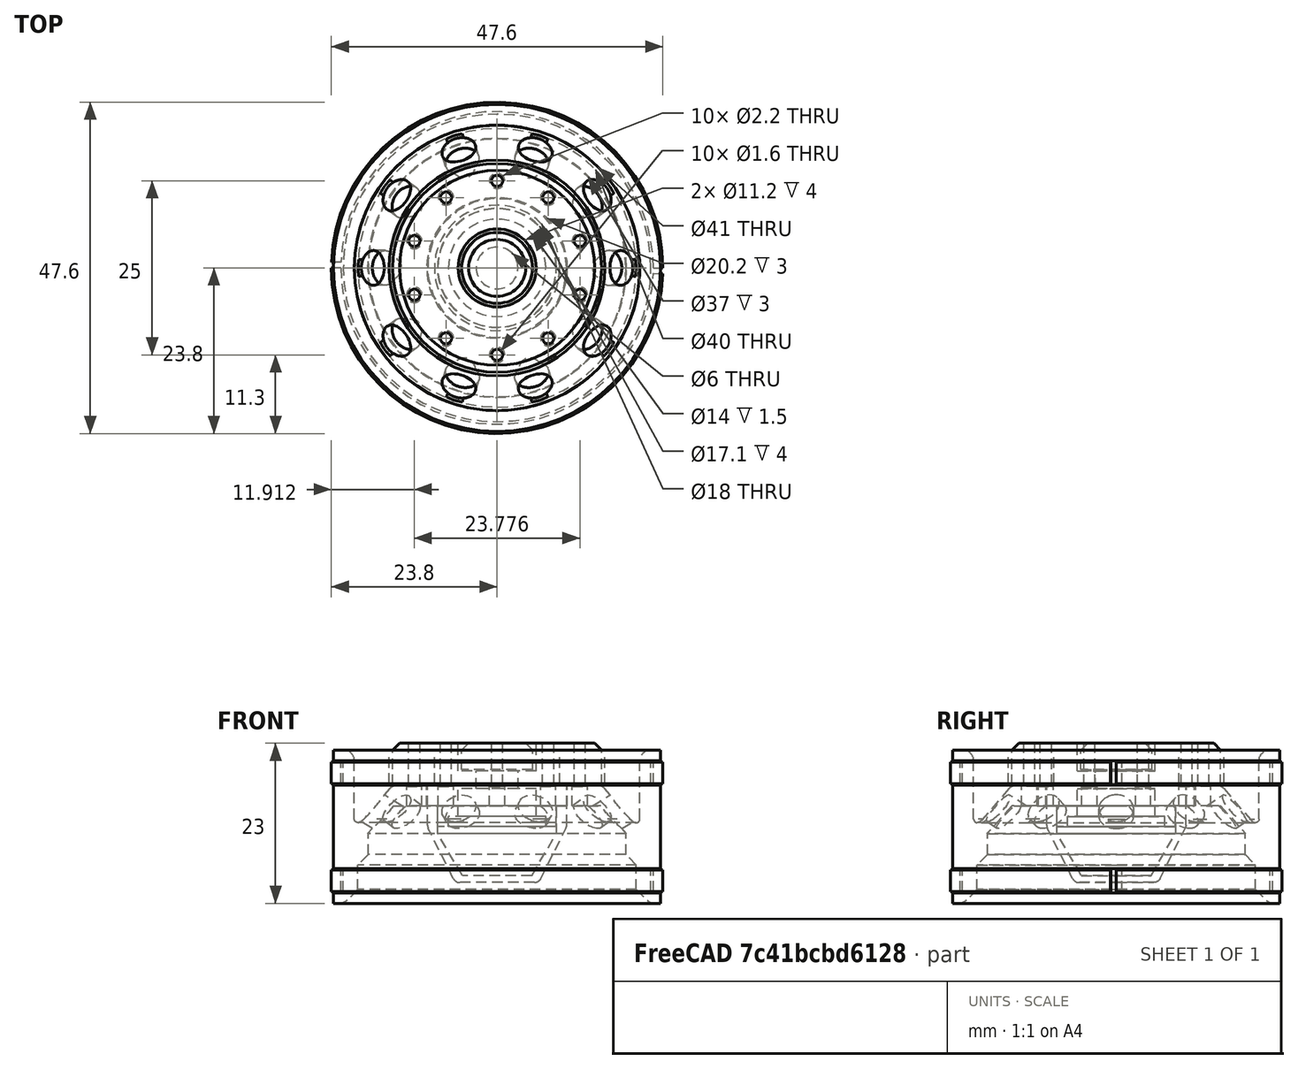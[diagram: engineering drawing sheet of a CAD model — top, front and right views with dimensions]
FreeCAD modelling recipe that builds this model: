
FCSTD DOCUMENT  (FreeCAD 0.19R)
Label: wheels-wide
License: All rights reserved
LicenseURL: http://en.wikipedia.org/wiki/All_rights_reserved
objects: Part::Cylinder×69, Part::MultiFuse×34, Part::Cut×23, Part::Mirroring×5, Part::Fillet×5, Part::Cone×4, Part::Chamfer×4, App::DocumentObjectGroup×1
note: 144 computed .brp shape members not serialized (recipe doc carries the construction recipe); baked Part::Feature solids carry a one-line shape summary decoded from their .brp

FEATURE [Part::Cylinder] Cylinder073
  Angle = 360
  AttacherType = Attacher::AttachEngine3D
  Height = 22
  Radius = 23.5
FEATURE [Part::Cylinder] Cylinder074
  Angle = 360
  AttacherType = Attacher::AttachEngine3D
  Height = 19
  Radius = 23.5
FEATURE [Part::Cylinder] Cylinder075
  Angle = 360
  AttacherType = Attacher::AttachEngine3D
  Height = 19
  Radius = 22.1
FEATURE [Part::Cut] Cut022
  Base = -> Cylinder074
  Placement = pos=(0,0,1.5) rot=(0,0,1;0rad)
  Refine = true
  Tool = -> Cylinder075
FEATURE [Part::Cut] Cut023
  Base = -> Cylinder073
  Refine = true
  Tool = -> Cut022
FEATURE [Part::Cylinder] Cylinder076
  Angle = 360
  AttacherType = Attacher::AttachEngine3D
  Height = 12
  Radius = 22
FEATURE [Part::Cylinder] Cylinder077
  Angle = 360
  AttacherType = Attacher::AttachEngine3D
  Height = 12
  Placement = pos=(0,0,0.5) rot=(0,0,1;0rad)
  Radius = 23.5
FEATURE [Part::Cut] Cut024
  Base = -> Cylinder077
  Placement = pos=(0,0,4.5) rot=(0,0,1;0rad)
  Refine = true
  Tool = -> Cylinder076
FEATURE [Part::Cylinder] Cylinder078
  Angle = 360
  AttacherType = Attacher::AttachEngine3D
  Height = 22
  Radius = 18.5
FEATURE [Part::MultiFuse] Fusion014
  Refine = true
  Shapes = -> [Cut024,Cut023]
FEATURE [Part::Cut] Cut025
  Base = -> Fusion014
  Refine = true
  Tool = -> Cylinder078
FEATURE [Part::Cone] Cone002
  Angle = 360
  AttacherType = Attacher::AttachEngine3D
  Height = 7
  Placement = pos=(0,0,15) rot=(0,0,1;0rad)
  Radius1 = 21
  Radius2 = 15
FEATURE [Part::Cylinder] Cylinder079
  Angle = 360
  AttacherType = Attacher::AttachEngine3D
  Height = 12
  Placement = pos=(0,0,10) rot=(0,0,1;0rad)
  Radius = 20.5
FEATURE [Part::Cylinder] Cylinder080
  Angle = 360
  AttacherType = Attacher::AttachEngine3D
  Height = 7
  Radius = 20
FEATURE [Part::Cylinder] Cylinder081
  Angle = 360
  AttacherType = Attacher::AttachEngine3D
  Height = 26
  Radius = 10
FEATURE [Part::Cylinder] Cylinder082
  Angle = 360
  AttacherType = Attacher::AttachEngine3D
  Height = 8
  Placement = pos=(12,0,16) rot=(0,1,0;1.01229rad)
  Radius = 2.5
FEATURE [Part::Mirroring] Part__Mirroring005  label="Cylinder107 (Mirror #1)009"
  Base = (0,0,0)
  Normal = (1,0,0)
  Source = -> Cylinder082
FEATURE [Part::Cylinder] Cylinder083
  Angle = 360
  AttacherType = Attacher::AttachEngine3D
  Height = 8
  Placement = pos=(12,0,16) rot=(0,1,0;1.01229rad)
  Radius = 2.5
FEATURE [Part::MultiFuse] Fusion015
  Refine = true
  Shapes = -> [Cylinder083,Part__Mirroring005]
FEATURE [Part::Cylinder] Cylinder084
  Angle = 360
  AttacherType = Attacher::AttachEngine3D
  Height = 8
  Placement = pos=(12,0,16) rot=(0,1,0;1.01229rad)
  Radius = 2.5
FEATURE [Part::Cylinder] Cylinder085
  Angle = 360
  AttacherType = Attacher::AttachEngine3D
  Height = 8
  Placement = pos=(12,0,16) rot=(0,1,0;1.01229rad)
  Radius = 2.5
FEATURE [Part::Mirroring] Part__Mirroring006  label="Cylinder107 (Mirror #1)010"
  Base = (0,0,0)
  Normal = (1,0,0)
  Source = -> Cylinder085
FEATURE [Part::MultiFuse] Fusion016
  Placement = pos=(0,0,0) rot=(0,0,1;0.628319rad)
  Refine = true
  Shapes = -> [Cylinder084,Part__Mirroring006]
FEATURE [Part::Cylinder] Cylinder086
  Angle = 360
  AttacherType = Attacher::AttachEngine3D
  Height = 8
  Placement = pos=(12,0,16) rot=(0,1,0;1.01229rad)
  Radius = 2.5
FEATURE [Part::Cylinder] Cylinder087
  Angle = 360
  AttacherType = Attacher::AttachEngine3D
  Height = 8
  Placement = pos=(12,0,16) rot=(0,1,0;1.01229rad)
  Radius = 2.5
FEATURE [Part::Mirroring] Part__Mirroring007  label="Cylinder107 (Mirror #1)011"
  Base = (0,0,0)
  Normal = (1,0,0)
  Source = -> Cylinder087
FEATURE [Part::MultiFuse] Fusion017
  Placement = pos=(0,0,0) rot=(0,0,1;1.25664rad)
  Refine = true
  Shapes = -> [Cylinder086,Part__Mirroring007]
FEATURE [Part::Cylinder] Cylinder088
  Angle = 360
  AttacherType = Attacher::AttachEngine3D
  Height = 8
  Placement = pos=(12,0,16) rot=(0,1,0;1.01229rad)
  Radius = 2.5
FEATURE [Part::Cylinder] Cylinder089
  Angle = 360
  AttacherType = Attacher::AttachEngine3D
  Height = 8
  Placement = pos=(12,0,16) rot=(0,1,0;1.01229rad)
  Radius = 2.5
FEATURE [Part::Mirroring] Part__Mirroring008  label="Cylinder107 (Mirror #1)012"
  Base = (0,0,0)
  Normal = (1,0,0)
  Source = -> Cylinder089
FEATURE [Part::MultiFuse] Fusion018
  Placement = pos=(0,0,0) rot=(0,0,1;1.88496rad)
  Refine = true
  Shapes = -> [Cylinder088,Part__Mirroring008]
FEATURE [Part::Cylinder] Cylinder090
  Angle = 360
  AttacherType = Attacher::AttachEngine3D
  Height = 8
  Placement = pos=(12,0,16) rot=(0,1,0;1.01229rad)
  Radius = 2.5
FEATURE [Part::Cylinder] Cylinder091
  Angle = 360
  AttacherType = Attacher::AttachEngine3D
  Height = 8
  Placement = pos=(12,0,16) rot=(0,1,0;1.01229rad)
  Radius = 2.5
FEATURE [Part::Mirroring] Part__Mirroring009  label="Cylinder107 (Mirror #1)013"
  Base = (0,0,0)
  Normal = (1,0,0)
  Source = -> Cylinder091
FEATURE [Part::MultiFuse] Fusion019
  Placement = pos=(0,0,0) rot=(0,0,1;2.51327rad)
  Refine = true
  Shapes = -> [Cylinder090,Part__Mirroring009]
FEATURE [Part::MultiFuse] Fusion020
  Placement = pos=(0,0,-6) rot=(0,0,1;0rad)
  Refine = true
  Shapes = -> [Fusion015,Fusion016,Fusion017,Fusion018,Fusion019]
FEATURE [Part::Cylinder] Cylinder092
  Angle = 360
  AttacherType = Attacher::AttachEngine3D
  Height = 10
  Placement = pos=(12.5,0,13) rot=(0,0,1;0rad)
  Radius = 1.1
FEATURE [Part::Cylinder] Cylinder093
  Angle = 360
  AttacherType = Attacher::AttachEngine3D
  Height = 10
  Placement = pos=(-12.5,0,13) rot=(0,0,1;0rad)
  Radius = 1.1
FEATURE [Part::MultiFuse] Fusion021
  Placement = pos=(0,0,0) rot=(0,0,1;0.314159rad)
  Refine = true
  Shapes = -> [Cylinder092,Cylinder093]
FEATURE [Part::Cylinder] Cylinder094
  Angle = 360
  AttacherType = Attacher::AttachEngine3D
  Height = 10
  Placement = pos=(12.5,0,13) rot=(0,0,1;0rad)
  Radius = 1.1
FEATURE [Part::Cylinder] Cylinder095
  Angle = 360
  AttacherType = Attacher::AttachEngine3D
  Height = 10
  Placement = pos=(-12.5,0,13) rot=(0,0,1;0rad)
  Radius = 1.1
FEATURE [Part::MultiFuse] Fusion022
  Placement = pos=(0,0,0) rot=(0,0,1;0.942478rad)
  Refine = true
  Shapes = -> [Cylinder094,Cylinder095]
FEATURE [Part::Cylinder] Cylinder096
  Angle = 360
  AttacherType = Attacher::AttachEngine3D
  Height = 10
  Placement = pos=(12.5,0,13) rot=(0,0,1;0rad)
  Radius = 1.1
FEATURE [Part::Cylinder] Cylinder097
  Angle = 360
  AttacherType = Attacher::AttachEngine3D
  Height = 10
  Placement = pos=(-12.5,0,13) rot=(0,0,1;0rad)
  Radius = 1.1
FEATURE [Part::MultiFuse] Fusion023
  Placement = pos=(0,0,0) rot=(0,0,1;1.5708rad)
  Refine = true
  Shapes = -> [Cylinder096,Cylinder097]
FEATURE [Part::Cylinder] Cylinder098
  Angle = 360
  AttacherType = Attacher::AttachEngine3D
  Height = 10
  Placement = pos=(12.5,0,13) rot=(0,0,1;0rad)
  Radius = 1.1
FEATURE [Part::Cylinder] Cylinder099
  Angle = 360
  AttacherType = Attacher::AttachEngine3D
  Height = 10
  Placement = pos=(-12.5,0,13) rot=(0,0,1;0rad)
  Radius = 1.1
FEATURE [Part::MultiFuse] Fusion024
  Placement = pos=(0,0,0) rot=(0,0,1;2.19911rad)
  Refine = true
  Shapes = -> [Cylinder098,Cylinder099]
FEATURE [Part::Cylinder] Cylinder100
  Angle = 360
  AttacherType = Attacher::AttachEngine3D
  Height = 10
  Placement = pos=(12.5,0,13) rot=(0,0,1;0rad)
  Radius = 1.1
FEATURE [Part::Cylinder] Cylinder101
  Angle = 360
  AttacherType = Attacher::AttachEngine3D
  Height = 10
  Placement = pos=(-12.5,0,13) rot=(0,0,1;0rad)
  Radius = 1.1
FEATURE [Part::MultiFuse] Fusion025
  Placement = pos=(0,0,0) rot=(0,0,1;2.82743rad)
  Refine = true
  Shapes = -> [Cylinder100,Cylinder101]
FEATURE [Part::MultiFuse] Fusion026
  Placement = pos=(0,0,-5) rot=(0,0,1;0rad)
  Refine = true
  Shapes = -> [Fusion021,Fusion022,Fusion025,Fusion024,Fusion023]
FEATURE [Part::Cone] Cone003
  Angle = 360
  AttacherType = Attacher::AttachEngine3D
  Height = 10
  Placement = pos=(0,0,9) rot=(0,0,1;0rad)
  Radius1 = 24
  Radius2 = 15
FEATURE [Part::Cut] Cut027
  Base = -> Cone002
  Refine = true
  Tool = -> Cylinder081
FEATURE [Part::Cut] Cut028
  Base = -> Cut027
  Placement = pos=(0,0,-5) rot=(0,0,1;0rad)
  Refine = true
  Tool = -> Cone003
FEATURE [Part::Cylinder] Cylinder102
  Angle = 360
  AttacherType = Attacher::AttachEngine3D
  Height = 26
  Radius = 10.1
FEATURE [Part::Cut] Cut029
  Base = -> Cut028
  Refine = true
  Tool = -> Fusion020
FEATURE [Part::Cut] Cut030
  Base = -> Cut029
  Refine = true
  Tool = -> Fusion026
FEATURE [Part::Cut] Cut031
  Base = -> Cut030
  Refine = true
  Tool = -> Cylinder102
FEATURE [Part::Fillet] Fillet003
  Base = -> Cut031
  Edges = 1 edges r=1.5: [Edge6]
FEATURE [Part::Cut] Cut032
  Base = -> Cut025
  Refine = true
  Tool = -> Cylinder080
FEATURE [Part::Cut] Cut033
  Base = -> Cut032
  Refine = true
  Tool = -> Cylinder079
FEATURE [Part::Chamfer] Chamfer002
  Base = -> Cut033
  Edges = 1 edges r=1.49: [Edge21]
FEATURE [Part::Chamfer] Chamfer003
  Base = -> Chamfer002
  Edges = 1 edges r=2: [Edge3]
FEATURE [Part::Fillet] Fillet004
  Base = -> Chamfer003
  Edges = 2 edges r=1.5: [Edge5,Edge19]
FEATURE [Part::Cylinder] Cylinder058
  Angle = 360
  AttacherType = Attacher::AttachEngine3D
  Height = 6
  Placement = pos=(0,0,9) rot=(0,0,1;0rad)
  Radius = 15
FEATURE [Part::Cylinder] Cylinder042
  Angle = 360
  AttacherType = Attacher::AttachEngine3D
  Height = 1.5
  Placement = pos=(0,0,3) rot=(0,0,1;0rad)
  Radius = 7
FEATURE [Part::Cylinder] Cylinder060
  Angle = 360
  AttacherType = Attacher::AttachEngine3D
  Height = 4
  Placement = pos=(0,0,6.5) rot=(0,0,1;0rad)
  Radius = 5.6
FEATURE [Part::Cylinder] Cylinder061
  Angle = 360
  AttacherType = Attacher::AttachEngine3D
  Height = 4
  Radius = 5.6
FEATURE [Part::Cylinder] Cylinder062
  Angle = 360
  AttacherType = Attacher::AttachEngine3D
  Height = 4
  Placement = pos=(0,0,3) rot=(0,0,1;0rad)
  Radius = 3
FEATURE [Part::MultiFuse] Fusion033
  Placement = pos=(0,0,4.5) rot=(0,0,1;0rad)
  Refine = true
  Shapes = -> [Cylinder060,Cylinder062,Cylinder061]
FEATURE [Part::Cylinder] Cylinder043
  Angle = 360
  AttacherType = Attacher::AttachEngine3D
  Height = 20
  Placement = pos=(12.5,0,13) rot=(0,0,1;0rad)
  Radius = 0.8
FEATURE [Part::Cylinder] Cylinder047
  Angle = 360
  AttacherType = Attacher::AttachEngine3D
  Height = 20
  Placement = pos=(12.5,0,13) rot=(0,0,1;0rad)
  Radius = 0.8
FEATURE [Part::Cylinder] Cylinder048
  Angle = 360
  AttacherType = Attacher::AttachEngine3D
  Height = 20
  Placement = pos=(-12.5,0,13) rot=(0,0,1;0rad)
  Radius = 0.8
FEATURE [Part::MultiFuse] Fusion035
  Placement = pos=(0,0,0) rot=(0,0,1;1.5708rad)
  Refine = true
  Shapes = -> [Cylinder047,Cylinder048]
FEATURE [Part::Cylinder] Cylinder045
  Angle = 360
  AttacherType = Attacher::AttachEngine3D
  Height = 20
  Placement = pos=(12.5,0,13) rot=(0,0,1;0rad)
  Radius = 0.8
FEATURE [Part::Cylinder] Cylinder044
  Angle = 360
  AttacherType = Attacher::AttachEngine3D
  Height = 20
  Placement = pos=(-12.5,0,13) rot=(0,0,1;0rad)
  Radius = 0.8
FEATURE [Part::MultiFuse] Fusion031
  Placement = pos=(0,0,0) rot=(0,0,1;0.314159rad)
  Refine = true
  Shapes = -> [Cylinder043,Cylinder044]
FEATURE [Part::Cylinder] Cylinder041
  Angle = 360
  AttacherType = Attacher::AttachEngine3D
  Height = 6
  Placement = pos=(0,0,3) rot=(0,0,1;0rad)
  Radius = 10
FEATURE [Part::Cylinder] Cylinder046
  Angle = 360
  AttacherType = Attacher::AttachEngine3D
  Height = 20
  Placement = pos=(-12.5,0,13) rot=(0,0,1;0rad)
  Radius = 0.8
FEATURE [Part::MultiFuse] Fusion028
  Placement = pos=(0,0,0) rot=(0,0,1;0.942478rad)
  Refine = true
  Shapes = -> [Cylinder045,Cylinder046]
FEATURE [Part::Cylinder] Cylinder051
  Angle = 360
  AttacherType = Attacher::AttachEngine3D
  Height = 20
  Placement = pos=(12.5,0,13) rot=(0,0,1;0rad)
  Radius = 0.8
FEATURE [Part::Cylinder] Cylinder052
  Angle = 360
  AttacherType = Attacher::AttachEngine3D
  Height = 20
  Placement = pos=(-12.5,0,13) rot=(0,0,1;0rad)
  Radius = 0.8
FEATURE [Part::MultiFuse] Fusion032
  Placement = pos=(0,0,0) rot=(0,0,1;2.82743rad)
  Refine = true
  Shapes = -> [Cylinder051,Cylinder052]
FEATURE [Part::Cylinder] Cylinder049
  Angle = 360
  AttacherType = Attacher::AttachEngine3D
  Height = 20
  Placement = pos=(12.5,0,13) rot=(0,0,1;0rad)
  Radius = 0.8
FEATURE [Part::Cylinder] Cylinder050
  Angle = 360
  AttacherType = Attacher::AttachEngine3D
  Height = 20
  Placement = pos=(-12.5,0,13) rot=(0,0,1;0rad)
  Radius = 0.8
FEATURE [Part::MultiFuse] Fusion034
  Placement = pos=(0,0,0) rot=(0,0,1;2.19911rad)
  Refine = true
  Shapes = -> [Cylinder049,Cylinder050]
FEATURE [Part::MultiFuse] Fusion036
  Placement = pos=(0,0,3) rot=(0,0,1;0rad)
  Refine = true
  Shapes = -> [Fusion031,Fusion028,Fusion032,Fusion034,Fusion035]
FEATURE [Part::MultiFuse] Fusion
  Refine = true
  Shapes = -> [Cylinder058,Cylinder041]
FEATURE [Part::Cut] Cut
  Base = -> Fusion
  Refine = true
  Tool = -> Cylinder042
FEATURE [Part::Cut] Cut034
  Base = -> Cut
  Placement = pos=(0,0,8) rot=(0,0,1;0rad)
  Refine = true
  Tool = -> Fusion033
FEATURE [Part::Cut] Cut035
  Base = -> Cut034
  Refine = true
  Tool = -> Fusion036
FEATURE [Part::Cylinder] Cylinder103
  Angle = 360
  AttacherType = Attacher::AttachEngine3D
  Height = 3
  Placement = pos=(0,0,11) rot=(0,0,1;0rad)
  Radius = 10
FEATURE [Part::Cylinder] Cylinder104
  Angle = 360
  AttacherType = Attacher::AttachEngine3D
  Height = 3
  Placement = pos=(0,0,11) rot=(0,0,1;0rad)
  Radius = 8.5
FEATURE [Part::Cut] Cut036
  Base = -> Cylinder103
  Refine = true
  Tool = -> Cylinder104
FEATURE [Part::Cut] Cut037
  Base = -> Cut035
  Refine = true
  Tool = -> Cut036
FEATURE [Part::Chamfer] Chamfer  label="hub-wide"
  Base = -> Cut037
  Edges = 1 edges r=1: [Edge1]
FEATURE [Part::Cylinder] Cylinder105
  Angle = 360
  AttacherType = Attacher::AttachEngine3D
  Height = 3
  Placement = pos=(0,0,11) rot=(0,0,1;0rad)
  Radius = 10
FEATURE [Part::Cylinder] Cylinder106
  Angle = 360
  AttacherType = Attacher::AttachEngine3D
  Height = 4
  Placement = pos=(0,0,10) rot=(0,0,1;0rad)
  Radius = 8.55
FEATURE [Part::Cone] Cone
  Angle = 360
  AttacherType = Attacher::AttachEngine3D
  Height = 8
  Placement = pos=(0,0,3) rot=(0,0,1;0rad)
  Radius1 = 6
  Radius2 = 10
FEATURE [Part::MultiFuse] Fusion037
  Refine = true
  Shapes = -> [Cone,Cylinder105]
FEATURE [Part::Cylinder] Cylinder066
  Angle = 178
  AttacherType = Attacher::AttachEngine3D
  Height = 3.1
  Placement = pos=(0,0,1.8) rot=(0,0,1;0rad)
  Radius = 23.8
FEATURE [Part::Cylinder] Cylinder067
  Angle = 360
  AttacherType = Attacher::AttachEngine3D
  Height = 17
  Radius = 22.45
FEATURE [Part::Cut] Cut016
  Base = -> Cylinder066
  Refine = true
  Tool = -> Cylinder067
FEATURE [Part::Cylinder] Cylinder068
  Angle = 178
  AttacherType = Attacher::AttachEngine3D
  Height = 3.1
  Placement = pos=(0,0,1.8) rot=(0,0,1;0rad)
  Radius = 23.8
FEATURE [Part::Cylinder] Cylinder069
  Angle = 360
  AttacherType = Attacher::AttachEngine3D
  Height = 17
  Radius = 22.45
FEATURE [Part::Cut] Cut017
  Base = -> Cylinder068
  Placement = pos=(0,0,0) rot=(0,0,1;3.14159rad)
  Refine = true
  Tool = -> Cylinder069
FEATURE [Part::MultiFuse] Fusion040
  Placement = pos=(0,0,15.4) rot=(0,0,1;0rad)
  Refine = true
  Shapes = -> [Cut016,Cut017]
FEATURE [Part::Cut] Cut018
  Base = -> Cylinder068
  Placement = pos=(0,0,0) rot=(0,0,1;3.14159rad)
  Refine = true
  Tool = -> Cylinder069
FEATURE [Part::Cut] Cut019
  Base = -> Cylinder066
  Refine = true
  Tool = -> Cylinder067
FEATURE [Part::MultiFuse] Fusion041
  Placement = pos=(0,0,-0.1) rot=(0,0,1;0rad)
  Refine = true
  Shapes = -> [Cut019,Cut018]
FEATURE [Part::MultiFuse] Fusion039  label="rim-support-lateral"
  Refine = true
  Shapes = -> [Fusion040,Fusion041]
FEATURE [Part::Cylinder] Cylinder070
  Angle = 360
  AttacherType = Attacher::AttachEngine3D
  Height = 4.8
  Placement = pos=(0,0,17.2) rot=(0,0,1;0rad)
  Radius = 15.5
FEATURE [Part::Cylinder] Cylinder109
  Angle = 360
  AttacherType = Attacher::AttachEngine3D
  Height = 3.8
  Radius = 5.1
FEATURE [Part::Chamfer] Chamfer006  label="hub-support"
  Base = -> Cylinder109
  Edges = 1 edges r=1: [Edge1]
  Placement = pos=(0,0,19.2) rot=(0,0,1;0rad)
FEATURE [Part::Cylinder] Cylinder110
  Angle = 360
  AttacherType = Attacher::AttachEngine3D
  Height = 4.8
  Placement = pos=(0,0,17.2) rot=(0,0,1;0rad)
  Radius = 9
FEATURE [Part::Cut] Cut039  label="rim-support"
  Base = -> Cylinder070
  Refine = true
  Tool = -> Cylinder110
FEATURE [Part::Cylinder] Cylinder111
  Angle = 360
  AttacherType = Attacher::AttachEngine3D
  Height = 0.2
  Placement = pos=(12.5,0,13) rot=(0,0,1;0rad)
  Radius = 1.1
FEATURE [Part::Cylinder] Cylinder112
  Angle = 360
  AttacherType = Attacher::AttachEngine3D
  Height = 0.2
  Placement = pos=(-12.5,0,13) rot=(0,0,1;0rad)
  Radius = 1.1
FEATURE [Part::MultiFuse] Fusion042
  Placement = pos=(0,0,0) rot=(0,0,1;0.314159rad)
  Refine = true
  Shapes = -> [Cylinder111,Cylinder112]
FEATURE [Part::Cylinder] Cylinder113
  Angle = 360
  AttacherType = Attacher::AttachEngine3D
  Height = 0.2
  Placement = pos=(12.5,0,13) rot=(0,0,1;0rad)
  Radius = 1.1
FEATURE [Part::Cylinder] Cylinder114
  Angle = 360
  AttacherType = Attacher::AttachEngine3D
  Height = 0.2
  Placement = pos=(-12.5,0,13) rot=(0,0,1;0rad)
  Radius = 1.1
FEATURE [Part::MultiFuse] Fusion043
  Placement = pos=(0,0,0) rot=(0,0,1;0.942478rad)
  Refine = true
  Shapes = -> [Cylinder113,Cylinder114]
FEATURE [Part::Cylinder] Cylinder115
  Angle = 360
  AttacherType = Attacher::AttachEngine3D
  Height = 0.2
  Placement = pos=(12.5,0,13) rot=(0,0,1;0rad)
  Radius = 1.1
FEATURE [Part::Cylinder] Cylinder116
  Angle = 360
  AttacherType = Attacher::AttachEngine3D
  Height = 0.2
  Placement = pos=(-12.5,0,13) rot=(0,0,1;0rad)
  Radius = 1.1
FEATURE [Part::MultiFuse] Fusion044
  Placement = pos=(0,0,0) rot=(0,0,1;1.5708rad)
  Refine = true
  Shapes = -> [Cylinder115,Cylinder116]
FEATURE [Part::Cylinder] Cylinder117
  Angle = 360
  AttacherType = Attacher::AttachEngine3D
  Height = 0.2
  Placement = pos=(12.5,0,13) rot=(0,0,1;0rad)
  Radius = 1.1
FEATURE [Part::Cylinder] Cylinder118
  Angle = 360
  AttacherType = Attacher::AttachEngine3D
  Height = 0.2
  Placement = pos=(-12.5,0,13) rot=(0,0,1;0rad)
  Radius = 1.1
FEATURE [Part::MultiFuse] Fusion045
  Placement = pos=(0,0,0) rot=(0,0,1;2.19911rad)
  Refine = true
  Shapes = -> [Cylinder117,Cylinder118]
FEATURE [Part::Cylinder] Cylinder119
  Angle = 360
  AttacherType = Attacher::AttachEngine3D
  Height = 0.2
  Placement = pos=(12.5,0,13) rot=(0,0,1;0rad)
  Radius = 1.1
FEATURE [Part::Cylinder] Cylinder120
  Angle = 360
  AttacherType = Attacher::AttachEngine3D
  Height = 0.2
  Placement = pos=(-12.5,0,13) rot=(0,0,1;0rad)
  Radius = 1.1
FEATURE [Part::MultiFuse] Fusion046
  Placement = pos=(0,0,0) rot=(0,0,1;2.82743rad)
  Refine = true
  Shapes = -> [Cylinder119,Cylinder120]
FEATURE [Part::MultiFuse] Fusion047  label="rim-support-holes"
  Placement = pos=(0,0,3.8) rot=(0,0,1;0rad)
  Refine = true
  Shapes = -> [Fusion042,Fusion043,Fusion046,Fusion045,Fusion044]
FEATURE [Part::Cylinder] Cylinder
  Angle = 360
  AttacherType = Attacher::AttachEngine3D
  Height = 1.6
  Placement = pos=(0,0,10) rot=(0,0,1;0rad)
  Radius = 21
FEATURE [Part::Cylinder] Cylinder121
  Angle = 360
  AttacherType = Attacher::AttachEngine3D
  Height = 1.6
  Placement = pos=(0,0,10) rot=(0,0,1;0rad)
  Radius = 19.5
FEATURE [Part::Cut] Cut040
  Base = -> Cylinder
  Refine = true
  Tool = -> Cylinder121
FEATURE [Part::MultiFuse] Fusion048
  Refine = true
  Shapes = -> [Fillet003,Cut040]
FEATURE [Part::Fillet] Fillet005
  Base = -> Fusion048
  Edges = 1 edges r=1: [Edge7]
FEATURE [Part::MultiFuse] Fusion049
  Refine = true
  Shapes = -> [Fillet004,Fillet005]
FEATURE [Part::Fillet] Fillet006  label="rim-wide"
  Base = -> Fusion049
  Edges = 1 edges r=0.5: [Edge215]
FEATURE [Part::Cone] Cone004
  Angle = 360
  AttacherType = Attacher::AttachEngine3D
  Height = 6
  Placement = pos=(0,0,4) rot=(0,0,1;0rad)
  Radius1 = 5
  Radius2 = 8.5
FEATURE [Part::MultiFuse] Fusion050
  Refine = true
  Shapes = -> [Cone004,Cylinder106]
FEATURE [Part::Cut] Cut041
  Base = -> Fusion037
  Refine = true
  Tool = -> Fusion050
FEATURE [Part::Fillet] Fillet  label="hub-wide-cap"
  Base = -> Cut041
  Edges = 2 edges r=1: [Edge1,Edge3]
FEATURE [App::DocumentObjectGroup] Group  label="Tools"
  Group = -> [Fusion039,Chamfer006,Cut039,Fusion047]
